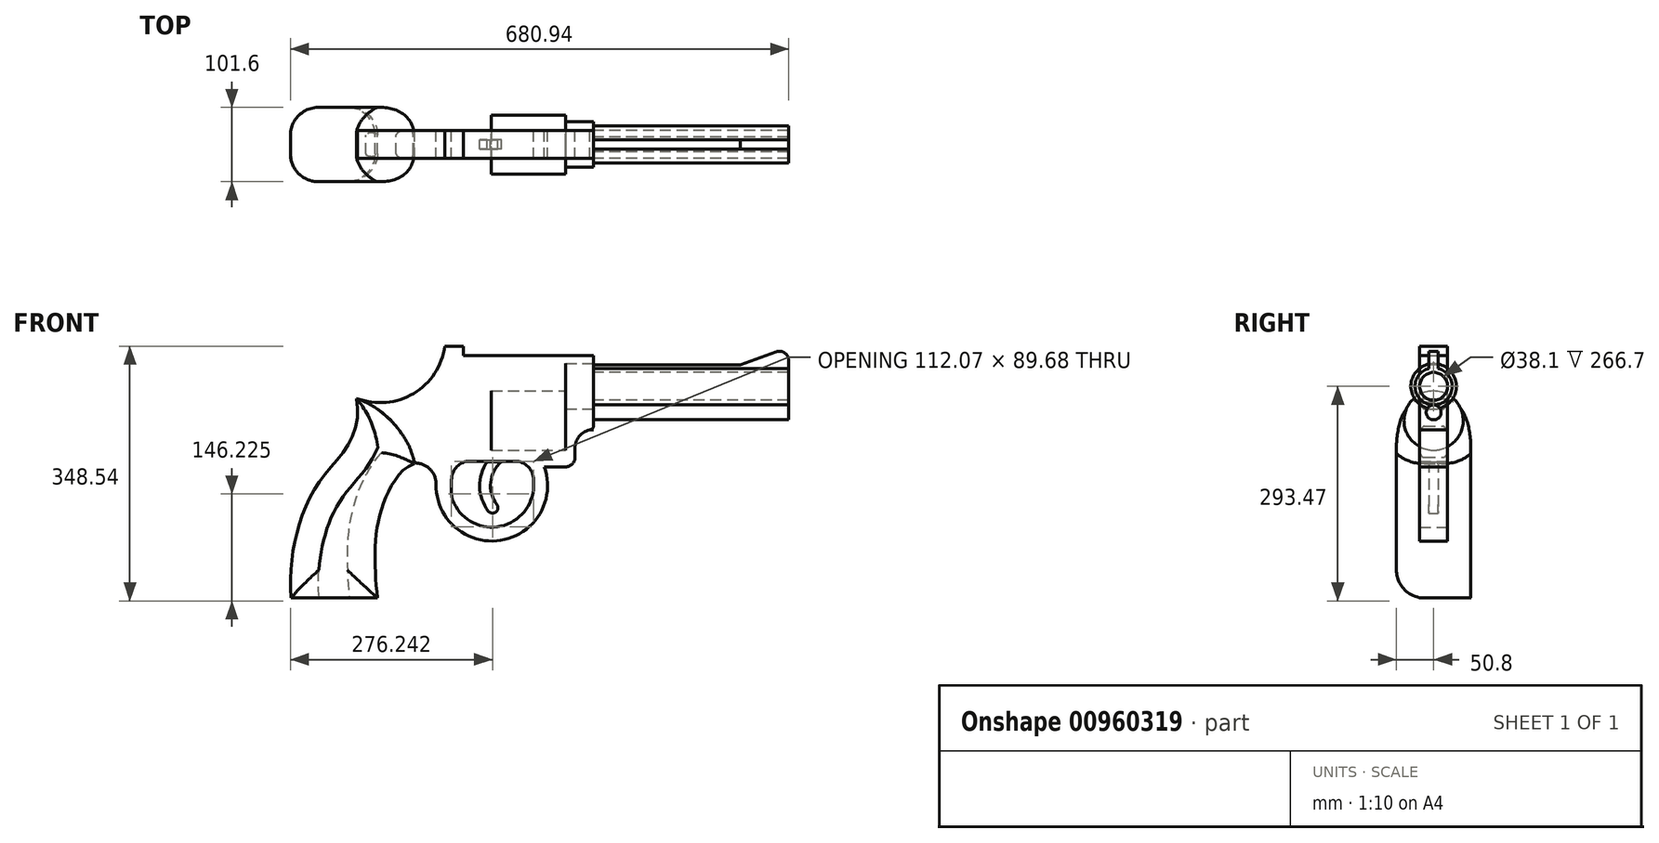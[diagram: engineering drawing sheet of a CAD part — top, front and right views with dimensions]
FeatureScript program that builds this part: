
annotation { "Feature Type Name" : "Feature", "Feature Type Description" : "" }
export const myFeature = defineFeature(function(context is Context, id is Id, definition is map)
    precondition{}
    {
        {
            var Q0;
            Q0=qCreatedBy(makeId("Right.planeOp"),FACE);
            var sketch = newSketch(context, id + "F0", { "sketchPlane" : qUnion([Q0])});
            skArc(sketch, "E0", {"start": v(-6.35, 265.9) * mm, "mid": v(0, 215.9) * mm, "end": v(6.35, 265.9) * mm});
            skCircle(sketch, "E1.0", {"center": v(0, 241.3) * mm, "radius": 19.05 * mm});
            skCircle(sketch, "E2", {"center": v(0, 205.74) * mm, "radius": 10.16 * mm});
            skLineSegment(sketch, "E3", {"start": v(-6.35, 265.9) * mm, "end": v(-6.35, 270.97) * mm});
            skLineSegment(sketch, "E4", {"start": v(-6.35, 270.97) * mm, "end": v(6.35, 270.97) * mm});
            skLineSegment(sketch, "E5", {"start": v(6.35, 270.97) * mm, "end": v(6.35, 265.9) * mm});
            skSolve(sketch);
        }
        {
            var Q0;
            Q0=makeQuery(id+"F0.imprint","IMPRINT",FACE,{"disambiguationData":[TD([[makeQuery(id+"F0.imprint","IMPRINT",EDGE,{"derivedFrom":sQuery(id+"F0.wireOp",EDGE,"E1.0")}),-1.0]])]});
            var Q1;
            {var subQ0=sQuery(id+"F0.wireOp",EDGE,"E2");Q1=makeQuery(id+"F0.imprint","IMPRINT",FACE,{"disambiguationData":[TD([[makeQuery(id+"F0.imprint","IMPRINT",EDGE,{"disambiguationData":[TD([[makeQuery(id+"F0.imprint","INTERSECT",VERTEX,{"derivedFrom":[sQuery(id+"F0.wireOp",EDGE,"E0"),subQ0]}),-1.0]])],"derivedFrom":subQ0}),1.0]])]});}
            extrude(context, id + "F1", {"entities" : qUnion([Q0, Q1]), "depth" : 215.9 * mm, "hasSecondDirection" : true, "secondDirectionOppositeDirection" : true, "secondDirectionDepth" : 50.8 * mm});
        }
        {
            var Q0;
            Q0=qCreatedBy(makeId("Front.planeOp"),FACE);
            var sketch = newSketch(context, id + "F2", { "sketchPlane" : qUnion([Q0])});
            skLineSegment(sketch, "E6", {"start": v(215.9, 270.97) * mm, "end": v(215.9, 276.75) * mm});
            skLineSegment(sketch, "E7", {"start": v(198.86, 288.68) * mm, "end": v(150.16, 270.97) * mm});
            skLineSegment(sketch, "E8", {"start": v(150.16, 270.97) * mm, "end": v(215.9, 270.97) * mm});
            skPoint(sketch, "E9.visualSharp", {"position": v(215.9, 294.88) * mm});
            skArc(sketch, "E9.filletArc", {"start": v(215.9, 276.75) * mm, "mid": v(210.49, 287.15) * mm, "end": v(198.86, 288.68) * mm});
            skSolve(sketch);
        }
        {
            var Q0;
            Q0=qSketchRegion(id+"F2",true);
            extrude(context, id + "F3", {"entities" : qUnion([Q0]), "operationType" : NewBodyOperationType.ADD, "oppositeDirection" : true, "depth" : 6.35 * mm, "hasSecondDirection" : true, "secondDirectionOppositeDirection" : false, "secondDirectionDepth" : 6.35 * mm});
        }
        {
            var Q0;
            Q0=qCreatedBy(makeId("Front.planeOp"),FACE);
            var sketch = newSketch(context, id + "F4", { "sketchPlane" : qUnion([Q0])});
            skLineSegment(sketch, "E10", {"start": v(-50.8, 270.97) * mm, "end": v(-50.8, 187.15) * mm});
            skLineSegment(sketch, "E11", {"start": v(-50.8, 182.07) * mm, "end": v(-55.88, 182.07) * mm});
            skLineSegment(sketch, "E12", {"start": v(-76.2, 156.67) * mm, "end": v(-76.2, 143.97) * mm});
            skLineSegment(sketch, "E13", {"start": v(-88.9, 131.27) * mm, "end": v(-117.91, 131.27) * mm});
            skPoint(sketch, "E14.visualSharp", {"position": v(-50.8, 182.07) * mm});
            skArc(sketch, "E14.filletArc", {"start": v(-55.88, 182.07) * mm, "mid": v(-52.29, 183.56) * mm, "end": v(-50.8, 187.15) * mm});
            skPoint(sketch, "E15.visualSharp", {"position": v(-76.2, 182.07) * mm});
            skArc(sketch, "E15.filletArc", {"start": v(-50.8, 182.07) * mm, "mid": v(-68.76, 174.63) * mm, "end": v(-76.2, 156.67) * mm});
            skPoint(sketch, "E16.visualSharp", {"position": v(-76.2, 131.27) * mm});
            skArc(sketch, "E16.filletArc", {"start": v(-88.9, 131.27) * mm, "mid": v(-79.92, 135) * mm, "end": v(-76.2, 143.97) * mm});
            skArc(sketch, "E17", {"start": v(-265.94, 107.45) * mm, "mid": v(-178.49, 30.51) * mm, "end": v(-117.36, 129.67) * mm});
            skArc(sketch, "E18", {"start": v(-243.18, 85.59) * mm, "mid": v(-182.27, 49.22) * mm, "end": v(-132.89, 100.16) * mm});
            skArc(sketch, "E19", {"start": v(-265.94, 107.45) * mm, "mid": v(-274.3, 128.17) * mm, "end": v(-295.08, 136.4) * mm});
            skLineSegment(sketch, "E20.bottom", {"start": v(-242.81, 101.61) * mm, "end": v(-246.74, 101.61) * mm});
            skLineSegment(sketch, "E20.top", {"start": v(-158.16, 138.9) * mm, "end": v(-219.44, 138.9) * mm});
            skLineSegment(sketch, "E20.left", {"start": v(-132.76, 102.7) * mm, "end": v(-132.76, 113.5) * mm});
            skLineSegment(sketch, "E20.right", {"start": v(-244.84, 94.6) * mm, "end": v(-244.84, 113.5) * mm});
            skArc(sketch, "E21.filletArc", {"start": v(-219.44, 138.9) * mm, "mid": v(-237.4, 131.45) * mm, "end": v(-244.84, 113.5) * mm});
            skArc(sketch, "E22.filletArc", {"start": v(-132.76, 113.5) * mm, "mid": v(-140.2, 131.45) * mm, "end": v(-158.16, 138.9) * mm});
            skArc(sketch, "E23.trimOffspring", {"start": v(-265.94, 107.45) * mm, "mid": v(-177.65, 30.64) * mm, "end": v(-117.91, 131.27) * mm});
            skArc(sketch, "E24.filletArc", {"start": v(-244.84, 94.6) * mm, "mid": v(-244.42, 90.02) * mm, "end": v(-243.18, 85.59) * mm});
            skPoint(sketch, "E25.visualSharp", {"position": v(-132.76, 101.61) * mm});
            skArc(sketch, "E25.filletArc", {"start": v(-132.89, 100.16) * mm, "mid": v(-132.8, 101.43) * mm, "end": v(-132.76, 102.7) * mm});
            skArc(sketch, "E26", {"start": v(-295.08, 136.4) * mm, "mid": v(-323.42, 190.23) * mm, "end": v(-373.53, 224.7) * mm});
            skArc(sketch, "E27", {"start": v(-373.53, 224.7) * mm, "mid": v(-296.43, 231.64) * mm, "end": v(-254, 296.37) * mm});
            skLineSegment(sketch, "E28", {"start": v(-254, 296.37) * mm, "end": v(-228.6, 296.37) * mm});
            skLineSegment(sketch, "E29", {"start": v(-228.6, 296.37) * mm, "end": v(-228.6, 283.67) * mm});
            skLineSegment(sketch, "E30", {"start": v(-228.6, 283.67) * mm, "end": v(-50.8, 283.67) * mm});
            skLineSegment(sketch, "E31", {"start": v(-50.8, 283.67) * mm, "end": v(-50.8, 270.97) * mm});
            skSolve(sketch);
        }
        {
            var Q0;
            Q0=qSketchRegion(id+"F4",true);
            var Q1;
            Q1=makeQuery(id+"F4.imprint","IMPRINT",FACE,{"disambiguationData":[TD([[makeQuery(id+"F4.imprint","IMPRINT",EDGE,{"derivedFrom":sQuery(id+"F4.wireOp",EDGE,"E10")}),-1.0]])]});
            extrude(context, id + "F5", {"entities" : qUnion([Q0, Q1]), "depth" : 19.05 * mm, "hasSecondDirection" : true, "secondDirectionOppositeDirection" : true, "secondDirectionDepth" : 19.05 * mm});
        }
        {
            var Q0;
            Q0=qCreatedBy(makeId("Front.planeOp"),FACE);
            var sketch = newSketch(context, id + "F6", { "sketchPlane" : qUnion([Q0])});
            skArc(sketch, "E32", {"start": v(-176.64, 138.15) * mm, "mid": v(-191.33, 110.15) * mm, "end": v(-182.84, 79.7) * mm});
            skArc(sketch, "E33", {"start": v(-196.32, 138.15) * mm, "mid": v(-206.34, 104.18) * mm, "end": v(-194.61, 70.75) * mm});
            skArc(sketch, "E34", {"start": v(-194.61, 70.75) * mm, "mid": v(-184.25, 69.34) * mm, "end": v(-182.84, 79.7) * mm});
            skLineSegment(sketch, "E35", {"start": v(-176.64, 138.15) * mm, "end": v(-196.32, 138.15) * mm});
            skSolve(sketch);
        }
        {
            var Q0;
            Q0=qSketchRegion(id+"F6",true);
            extrude(context, id + "F7", {"entities" : qUnion([Q0]), "depth" : 6.35 * mm, "hasSecondDirection" : true, "secondDirectionOppositeDirection" : true, "secondDirectionDepth" : 6.35 * mm});
        }
        {
            var Q0;
            Q0=qCreatedBy(makeId("Right.planeOp"),FACE);
            var sketch = newSketch(context, id + "F8", { "sketchPlane" : qUnion([Q0])});
            skCircle(sketch, "E36", {"center": v(0, 241.31) * mm, "radius": 31.06 * mm});
            skSolve(sketch);
        }
        {
            var Q0;
            Q0=qSketchRegion(id+"F8",true);
            extrude(context, id + "F9", {"entities" : qUnion([Q0]), "oppositeDirection" : true, "depth" : 38.1 * mm});
        }
        {
            var Q0;
            Q0=makeQuery(id+"F9.opExtrude","SWEPT_BODY",BODY,{"disambiguationData":[OSD([sQuery(id+"F8.wireOp",EDGE,"E36")])]});
            var Q1;
            Q1=qCreatedBy(makeId("Right.planeOp"),FACE);
            transform(context, id + "F10", {"entities" : qUnion([Q0]), "transformType" : TransformType.TRANSLATION_DISTANCE, "transformDirection" : qUnion([Q1]), "distance" : 50.8 * mm, "oppositeDirection" : true, "makeCopy" : false});
        }
        {
            var Q0;
            Q0=qCreatedBy(makeId("Right.planeOp"),FACE);
            var sketch = newSketch(context, id + "F11", { "sketchPlane" : qUnion([Q0])});
            skCircle(sketch, "E37", {"center": v(0, 194.45) * mm, "radius": 40.5 * mm});
            skSolve(sketch);
        }
        {
            var Q0;
            Q0=makeQuery(id+"F11.imprint","IMPRINT",FACE,{"disambiguationData":[TD([[makeQuery(id+"F11.imprint","IMPRINT",EDGE,{"derivedFrom":sQuery(id+"F11.wireOp",EDGE,"E37")}),1.0]])]});
            extrude(context, id + "F12", {"entities" : qUnion([Q0]), "oppositeDirection" : true, "depth" : 101.6 * mm});
        }
        {
            var Q0;
            Q0=makeQuery(id+"F12.opExtrude","SWEPT_BODY",BODY,{"disambiguationData":[OSD([sQuery(id+"F11.wireOp",EDGE,"E37")])]});
            var Q1;
            Q1=qCreatedBy(makeId("Right.planeOp"),FACE);
            transform(context, id + "F13", {"entities" : qUnion([Q0]), "transformType" : TransformType.TRANSLATION_DISTANCE, "transformDirection" : qUnion([Q1]), "distance" : 88.9 * mm, "oppositeDirection" : true, "makeCopy" : false});
        }
        {
            var Q0;
            Q0=qCreatedBy(makeId("Right.planeOp"),FACE);
            var sketch = newSketch(context, id + "F14", { "sketchPlane" : qUnion([Q0])});
            skLineSegment(sketch, "E38", {"start": v(0, 248.2) * mm, "end": v(0, 140.16) * mm, "construction": true});
            skArc(sketch, "E39", {"start": v(0, 153.18) * mm, "mid": v(40.47, 193.65) * mm, "end": v(0, 234.12) * mm});
            skPoint(sketch, "E40.orphan", {"position": v(0, 231.17) * mm});
            skPoint(sketch, "E41.orphan", {"position": v(0, 156.13) * mm});
            skSolve(sketch);
        }
        {
            var Q0;
            Q0=qSketchRegion(id+"F14",true);
            var Q1;
            Q1=sQuery(id+"F14.wireOp",EDGE,"E39");
            var Q2;
            Q2=sQuery(id+"F14.wireOp",EDGE,"E38");
            revolve(context, id + "F15", {"bodyType" : ToolBodyType.SURFACE, "entities" : qUnion([Q0]), "surfaceEntities" : qUnion([Q1]), "axis" : qUnion([Q2]), "revolveType" : RevolveType.ONE_DIRECTION, "oppositeDirection" : true, "angle" : 180 * degree});
        }
        {
            var Q0;
            Q0=makeQuery(id+"F15.opRevolve","SWEPT_BODY",BODY,{"disambiguationData":[OSD([sQuery(id+"F14.wireOp",EDGE,"E39")])]});
            var Q1;
            Q1=qCreatedBy(makeId("Right.planeOp"),FACE);
            transform(context, id + "F16", {"entities" : qUnion([Q0]), "transformType" : TransformType.TRANSLATION_DISTANCE, "transformDirection" : qUnion([Q1]), "distance" : 203.2 * mm, "oppositeDirection" : true, "makeCopy" : false});
        }
        {
            var Q0;
            Q0=makeQuery(id+"F15.opRevolve","SWEPT_BODY",BODY,{"disambiguationData":[OSD([sQuery(id+"F14.wireOp",EDGE,"E39")])]});
            var Q1;
            Q1=qCreatedBy(makeId("Right.planeOp"),FACE);
            transform(context, id + "F17", {"entities" : qUnion([Q0]), "transformType" : TransformType.TRANSLATION_DISTANCE, "transformDirection" : qUnion([Q1]), "distance" : 12.7 * mm, "makeCopy" : false});
        }
        {
            var Q0;
            Q0=makeQuery(id+"F15.opRevolve","SWEPT_BODY",BODY,{"disambiguationData":[OSD([sQuery(id+"F14.wireOp",EDGE,"E39")])]});
            var Q1;
            Q1=qCreatedBy(makeId("Right.planeOp"),FACE);
            transform(context, id + "F18", {"entities" : qUnion([Q0]), "transformType" : TransformType.TRANSLATION_DISTANCE, "transformDirection" : qUnion([Q1]), "distance" : 6.35 * mm, "oppositeDirection" : true, "makeCopy" : false});
        }
        {
            var Q0;
            Q0=qCreatedBy(makeId("Front.planeOp"),FACE);
            var sketch = newSketch(context, id + "F19", { "sketchPlane" : qUnion([Q0])});
            skFitSpline(sketch, "E42", {"points": [v(-295.97, 135.37) * mm, v(-315.66, 121.53) * mm, v(-342.8, 65.11) * mm, v(-349.2, 0) * mm, v(-346, -48.26) * mm], "startDerivative": vector(-116.91, -52.78) * mm, "endDerivative": vector(18.49, -146.52) * mm});
            skFitSpline(sketch, "E43", {"points": [v(-374.74, 224.25) * mm, v(-374.21, 193.38) * mm, v(-388.05, 158.26) * mm, v(-413.74, 126.05) * mm, v(-448.96, 64.85) * mm, v(-463.97, -47.74) * mm], "startDerivative": vector(25.4, -198.34) * mm, "endDerivative": vector(39.5, -350.92) * mm});
            skLineSegment(sketch, "E44", {"start": v(-463.97, -47.74) * mm, "end": v(-346, -48.26) * mm});
            skFitSpline(sketch, "E45", {"points": [v(-374.74, 224.25) * mm, v(-332.33, 198.8) * mm, v(-295.97, 135.37) * mm], "startDerivative": vector(113.06, -31.02) * mm, "endDerivative": vector(12.54, -151.1) * mm});
            skSolve(sketch);
        }
        {
            var Q0;
            Q0=makeQuery(id+"F19.imprint","IMPRINT",FACE,{"disambiguationData":[TD([[makeQuery(id+"F19.imprint","IMPRINT",EDGE,{"derivedFrom":sQuery(id+"F19.wireOp",EDGE,"E42")}),-1.0]])]});
            extrude(context, id + "F20", {"entities" : qUnion([Q0]), "operationType" : NewBodyOperationType.ADD, "depth" : 50.8 * mm, "hasSecondDirection" : true, "secondDirectionOppositeDirection" : true, "secondDirectionDepth" : 50.8 * mm});
        }
        {
            var Q0;
            Q0=makeQuery(id+"F20.opExtrude","CAP_EDGE",EDGE,{"disambiguationData":[OSD([sQuery(id+"F19.wireOp",EDGE,"E43")])],"isStart":true});
            var Q1;
            Q1=makeQuery(id+"F20.opExtrude","CAP_EDGE",EDGE,{"disambiguationData":[OSD([sQuery(id+"F19.wireOp",EDGE,"E45")])],"isStart":true});
            var Q2;
            Q2=makeQuery(id+"F20.opExtrude","CAP_EDGE",EDGE,{"disambiguationData":[OSD([sQuery(id+"F19.wireOp",EDGE,"E42")])],"isStart":true});
            var Q3;
            Q3=makeQuery(id+"F20.opExtrude","CAP_EDGE",EDGE,{"disambiguationData":[OSD([sQuery(id+"F19.wireOp",EDGE,"E43")])],"isStart":false});
            var Q4;
            Q4=makeQuery(id+"F20.opExtrude","CAP_FACE",FACE,{"disambiguationData":[OSD([sQuery(id+"F19.wireOp",EDGE,"E42"),sQuery(id+"F19.wireOp",EDGE,"E43"),sQuery(id+"F19.wireOp",EDGE,"E44"),sQuery(id+"F19.wireOp",EDGE,"E45")])],"isStart":false});
            var Q5;
            Q5=makeQuery(id+"F20.opExtrude","CAP_EDGE",EDGE,{"disambiguationData":[OSD([sQuery(id+"F19.wireOp",EDGE,"E42")])],"isStart":false});
            fillet(context, id + "F21", {"entities" : qUnion([Q0, Q1, Q2, Q3, Q4, Q5]), "radius" : 38.1 * mm, "tangentPropagation" : true, "allowEdgeOverflow" : false});
        }
    });
